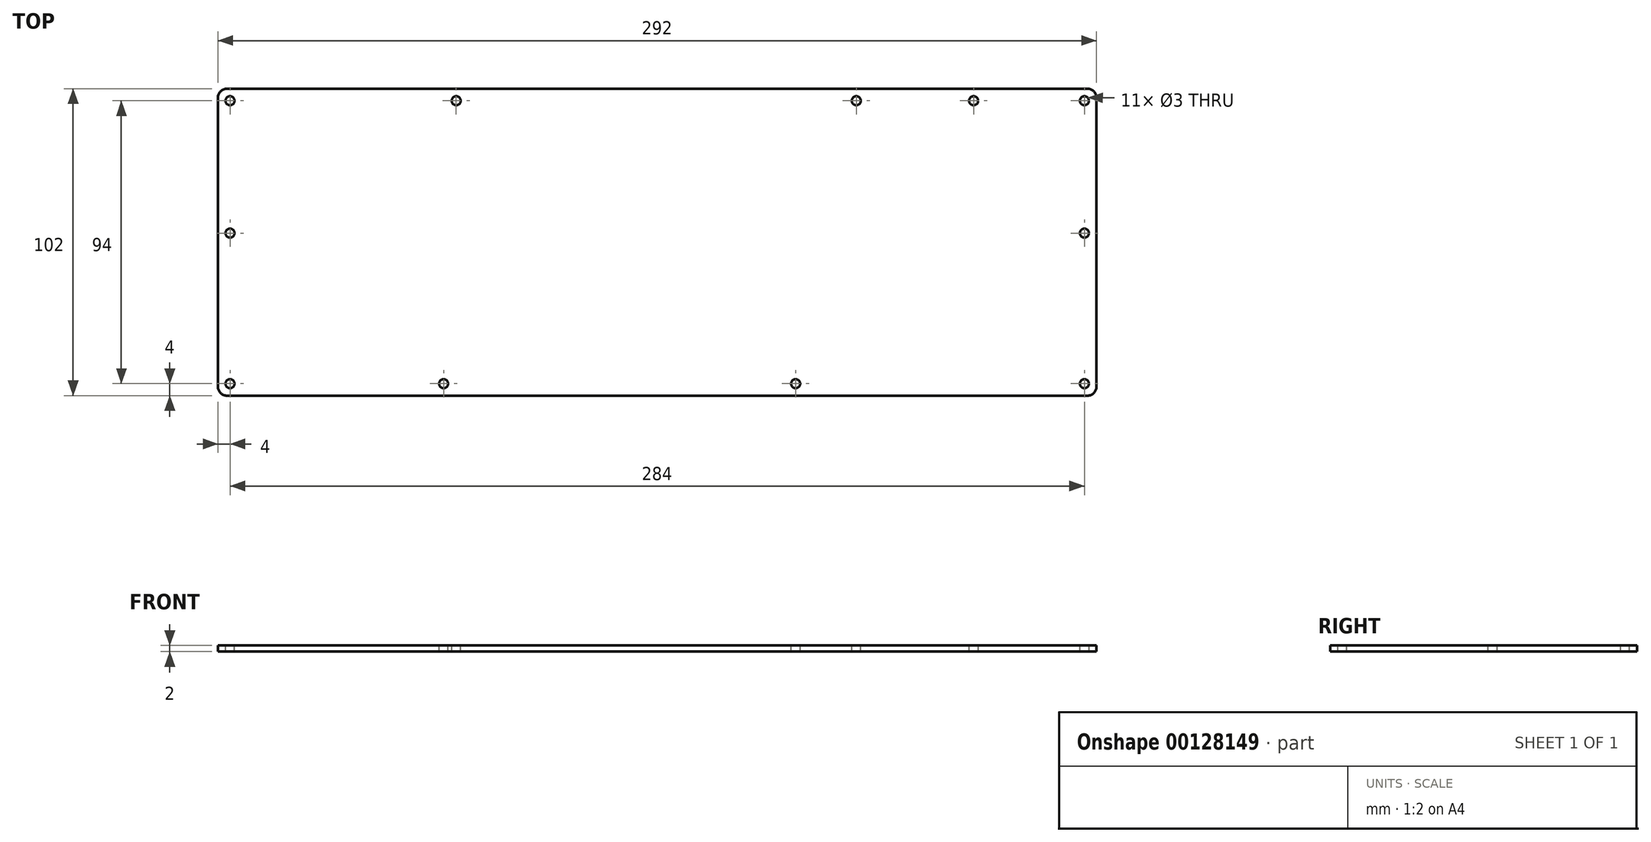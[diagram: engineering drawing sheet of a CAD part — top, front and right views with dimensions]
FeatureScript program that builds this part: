
annotation { "Feature Type Name" : "Feature", "Feature Type Description" : "" }
export const myFeature = defineFeature(function(context is Context, id is Id, definition is map)
    precondition{}
    {
        {
            var Q0;
            Q0=qCreatedBy(makeId("Top.planeOp"),FACE);
            var sketch = newSketch(context, id + "F0", { "sketchPlane" : qUnion([Q0])});
            skLineSegment(sketch, "E0.bottom", {"start": v(143, 51) * mm, "end": v(-143, 51) * mm});
            skLineSegment(sketch, "E0.top", {"start": v(143, -51) * mm, "end": v(-143, -51) * mm});
            skLineSegment(sketch, "E0.left", {"start": v(146, 48) * mm, "end": v(146, -48) * mm});
            skLineSegment(sketch, "E0.right", {"start": v(-146, 48) * mm, "end": v(-146, -48) * mm});
            skPoint(sketch, "E1.visualSharp", {"position": v(-146, 51) * mm});
            skArc(sketch, "E1.filletArc", {"start": v(-143, 51) * mm, "mid": v(-145.12, 50.12) * mm, "end": v(-146, 48) * mm});
            skPoint(sketch, "E2.visualSharp", {"position": v(-146, -51) * mm});
            skArc(sketch, "E2.filletArc", {"start": v(-146, -48) * mm, "mid": v(-145.12, -50.12) * mm, "end": v(-143, -51) * mm});
            skPoint(sketch, "E3.visualSharp", {"position": v(146, -51) * mm});
            skArc(sketch, "E3.filletArc", {"start": v(143, -51) * mm, "mid": v(145.12, -50.12) * mm, "end": v(146, -48) * mm});
            skArc(sketch, "E4.filletArc", {"start": v(146, 48) * mm, "mid": v(145.12, 50.12) * mm, "end": v(143, 51) * mm});
            skSolve(sketch);
        }
        {
            var Q0;
            Q0=qSketchRegion(id+"F0",true);
            extrude(context, id + "F1", {"entities" : qUnion([Q0]), "depth" : 2 * mm});
        }
        {
            var Q0;
            Q0=makeQuery(id+"F1.opExtrude","CAP_FACE",FACE,{"disambiguationData":[OSD([sQuery(id+"F0.wireOp",EDGE,"b1609128-1e4d-4f99-a9c0-d1eb6efb653b"),sQuery(id+"F0.wireOp",EDGE,"f4566b4f-cb64-43fb-b69e-2d4997d02e9e"),sQuery(id+"F0.wireOp",EDGE,"c58de4d6-b1a3-4d1c-92d8-0e596c6fe70e"),sQuery(id+"F0.wireOp",EDGE,"5249d06f-5fa9-4bc2-861d-4cda040d6d12"),sQuery(id+"F0.wireOp",EDGE,"a85e44d5-a424-4784-8d57-3f87bcd3cb1f"),sQuery(id+"F0.wireOp",EDGE,"26f2ad72-3e01-41bb-a775-2f8cfdfabe7d"),sQuery(id+"F0.wireOp",EDGE,"58a866ff-a5cd-410d-a599-dedaca65d45f"),sQuery(id+"F0.wireOp",EDGE,"ffbf0b70-5c72-4423-8b02-8f3d0a3b2328"),sQuery(id+"F0.wireOp",EDGE,"7f67b6f4-1288-461f-aa79-609977e3f21a"),sQuery(id+"F0.wireOp",EDGE,"55541f8a-b999-41dc-948e-6a4feb6e2708"),sQuery(id+"F0.wireOp",EDGE,"6f56692b-9edc-44ed-85e6-53072711c858"),sQuery(id+"F0.wireOp",EDGE,"d64ee7ec-02fb-4461-892d-8620c137c8be"),sQuery(id+"F0.wireOp",EDGE,"a331adab-5858-4e06-9c1d-1ebd579e2d6c"),sQuery(id+"F0.wireOp",EDGE,"872b245d-4d85-40be-bc62-1036af002ab7"),sQuery(id+"F0.wireOp",EDGE,"5f5c10bb-96b1-40b4-bf40-71e8b90fd5b4"),sQuery(id+"F0.wireOp",EDGE,"070c8fee-8489-4fd5-82cc-431f9b446bf5"),sQuery(id+"F0.wireOp",EDGE,"0514bdef-a2e6-47cc-91cb-2d3d024f583d"),sQuery(id+"F0.wireOp",EDGE,"38748b5d-75be-4e41-86c7-7b4e33a636ad"),sQuery(id+"F0.wireOp",EDGE,"ef5fee99-fa31-4ebf-9718-ae6e1dd8c854"),sQuery(id+"F0.wireOp",EDGE,"33aefef2-9a3a-4597-9de5-3f6917e2cb92"),sQuery(id+"F0.wireOp",EDGE,"f576047e-5c30-44eb-8430-c6ba2e10f578"),sQuery(id+"F0.wireOp",EDGE,"5237e12e-b54f-4000-b0ec-e2a188ff4113"),sQuery(id+"F0.wireOp",EDGE,"39a89d85-1c88-4538-9ca2-57a00aa53215"),sQuery(id+"F0.wireOp",EDGE,"1d3d1f3f-65d5-432a-a24c-25425600a27e"),sQuery(id+"F0.wireOp",EDGE,"65133dcd-ba31-495c-9030-11ebdab85244"),sQuery(id+"F0.wireOp",EDGE,"59442c7d-f29c-40c5-8460-04e0c5612805"),sQuery(id+"F0.wireOp",EDGE,"7c508e6d-ace5-438d-ae87-594742bffb03"),sQuery(id+"F0.wireOp",EDGE,"96358abd-ade1-4970-8e96-f48957cb49a9"),sQuery(id+"F0.wireOp",EDGE,"beaf586f-d415-4bcd-bc2c-fe17f6c56d29"),sQuery(id+"F0.wireOp",EDGE,"0b1e909e-c7ab-4355-90a4-b9d381122b20"),sQuery(id+"F0.wireOp",EDGE,"07e25036-969a-447a-8387-7472eab81c53"),sQuery(id+"F0.wireOp",EDGE,"4ac198d4-a843-4e16-ab13-53b4b61c7ec9"),sQuery(id+"F0.wireOp",EDGE,"5899e998-bb7d-4984-919d-5380da3ef46d"),sQuery(id+"F0.wireOp",EDGE,"85bf5025-0c0a-493d-8fd5-15a1002b9e1f"),sQuery(id+"F0.wireOp",EDGE,"433a8b32-5078-4fa2-bccb-dd94966a19e2"),sQuery(id+"F0.wireOp",EDGE,"ca2aed50-1aac-4a88-af60-10e4d26c56ce"),sQuery(id+"F0.wireOp",EDGE,"ad785477-14a5-48c7-ba58-707c46f4f765"),sQuery(id+"F0.wireOp",EDGE,"7e877f2a-03cb-4247-a0d1-3f1f17d45f2e"),sQuery(id+"F0.wireOp",EDGE,"5549e225-b8b0-41a5-a1f6-3a747b09e555"),sQuery(id+"F0.wireOp",EDGE,"7757f798-a692-4454-bd86-5a4d4f9a0c34"),sQuery(id+"F0.wireOp",EDGE,"3016f92a-8452-4434-919c-4a7fc7338035"),sQuery(id+"F0.wireOp",EDGE,"898612aa-0cec-428b-94af-f86252429d12"),sQuery(id+"F0.wireOp",EDGE,"a17dd576-292f-4e6b-9663-d9180f696670"),sQuery(id+"F0.wireOp",EDGE,"cbfd38bd-20b5-4d44-be8c-a17f12e052e0"),sQuery(id+"F0.wireOp",EDGE,"70ab0708-ffdb-4529-bf9e-4018cae3591c"),sQuery(id+"F0.wireOp",EDGE,"f406bcac-c7ef-481d-8174-8bc63e706a56"),sQuery(id+"F0.wireOp",EDGE,"dc331ac5-7670-45e9-89c7-03810e187fe8"),sQuery(id+"F0.wireOp",EDGE,"b3191053-ceed-4c24-bda0-5a50d567a071"),sQuery(id+"F0.wireOp",EDGE,"e110f5b5-6a02-4a34-82cf-196097ccbeb4"),sQuery(id+"F0.wireOp",EDGE,"2b5f7b66-3d2f-406f-a6d7-9a85497eda15"),sQuery(id+"F0.wireOp",EDGE,"76b1751e-cd68-4467-988c-686db3de7683"),sQuery(id+"F0.wireOp",EDGE,"16c5760e-34d5-4e50-8f9d-3caf3d151e1b"),sQuery(id+"F0.wireOp",EDGE,"d295ed9f-bfde-424d-aa21-20497ae6f13c"),sQuery(id+"F0.wireOp",EDGE,"ec12ba42-fae9-4e41-9ad7-bf38757b17f0"),sQuery(id+"F0.wireOp",EDGE,"7436cc0e-6ec4-46fe-a53e-8bd212bcf723"),sQuery(id+"F0.wireOp",EDGE,"0cedb4c9-6a6c-43c2-9996-506471cd3255"),sQuery(id+"F0.wireOp",EDGE,"ec54193d-d4cb-4b1f-86fc-2851957baaba"),sQuery(id+"F0.wireOp",EDGE,"4488f506-9ef2-4267-a6cf-a7b00e78e843"),sQuery(id+"F0.wireOp",EDGE,"372820ab-3034-42cd-b4e6-65ef871f9c40"),sQuery(id+"F0.wireOp",EDGE,"6573e008-ca1a-4dee-91fb-cecced364ef1"),sQuery(id+"F0.wireOp",EDGE,"0ea65bf7-9227-4dbe-9352-82978ca5b32e"),sQuery(id+"F0.wireOp",EDGE,"b1bb12b1-79df-4f2c-a40f-21d0aa567c24"),sQuery(id+"F0.wireOp",EDGE,"0c1536de-d6b0-46e4-9ba7-2841298be202"),sQuery(id+"F0.wireOp",EDGE,"207e1af1-11f0-4a44-9182-2a9f56c0d657"),sQuery(id+"F0.wireOp",EDGE,"27c13fe8-c982-4180-82e1-206dc62b37cb"),sQuery(id+"F0.wireOp",EDGE,"df3f2611-b4d2-4e5e-a9a9-9197ed178f10"),sQuery(id+"F0.wireOp",EDGE,"67ca35e5-e03d-4edf-9133-55c0f28c00dd"),sQuery(id+"F0.wireOp",EDGE,"211b09a9-55cd-462d-ac42-8101b668ed7f"),sQuery(id+"F0.wireOp",EDGE,"3790da84-eb6b-418a-b30a-773cb8711b72"),sQuery(id+"F0.wireOp",EDGE,"8ad775da-4dcc-4f57-b984-0bd12b45c958"),sQuery(id+"F0.wireOp",EDGE,"46f09f23-81b2-4bbc-9572-84064063ea46"),sQuery(id+"F0.wireOp",EDGE,"375117c6-4bbc-4c16-b11f-bde5a02c8ddd"),sQuery(id+"F0.wireOp",EDGE,"edf3fd68-21bd-4dda-b02f-30e2386ebe8c"),sQuery(id+"F0.wireOp",EDGE,"e9b376d0-4e66-4361-894a-f7f99b0a4dba"),sQuery(id+"F0.wireOp",EDGE,"7deef6e9-a95f-4fef-90d6-14df86437aaf"),sQuery(id+"F0.wireOp",EDGE,"3a2c3b9f-72e5-46fb-b22f-c3b3668238e3"),sQuery(id+"F0.wireOp",EDGE,"ef61160d-285f-4999-b3d1-3ad131a5c696"),sQuery(id+"F0.wireOp",EDGE,"5e485a8d-fc2c-447f-9fb7-2a8e8f7db1b8"),sQuery(id+"F0.wireOp",EDGE,"be4b73c1-2188-4d56-b092-b0e9aa332c99"),sQuery(id+"F0.wireOp",EDGE,"7886a41d-8e50-4074-9c4a-38b5df8d299c"),sQuery(id+"F0.wireOp",EDGE,"4e7a6acf-1550-41f7-a348-87a73df4ade2"),sQuery(id+"F0.wireOp",EDGE,"3075fc72-2a9a-4c54-a333-3b9aff6871ba"),sQuery(id+"F0.wireOp",EDGE,"1b470988-ea39-4ef3-b94f-c351ab6970c0"),sQuery(id+"F0.wireOp",EDGE,"d5d0fb32-3312-47e0-b08e-500f4e3a8d6f"),sQuery(id+"F0.wireOp",EDGE,"c95a7a57-a701-41e8-a435-0717771ea27e"),sQuery(id+"F0.wireOp",EDGE,"72f5413f-f806-4961-a1f2-17e8c49a2dbe"),sQuery(id+"F0.wireOp",EDGE,"12295bb0-ec03-4baf-b844-216b01d10c7f"),sQuery(id+"F0.wireOp",EDGE,"ea74abaf-c7a4-4655-a14d-8def43b58c3b"),sQuery(id+"F0.wireOp",EDGE,"fc38e52a-d66c-41f3-a18f-2ab74fc9a3aa"),sQuery(id+"F0.wireOp",EDGE,"b9a872e7-607d-4140-9fac-37e865748f2f"),sQuery(id+"F0.wireOp",EDGE,"469ab4fc-23a3-4a44-8d10-edb1ebb05813"),sQuery(id+"F0.wireOp",EDGE,"6c8f3efd-a16e-4969-a36d-9367de4a04a8"),sQuery(id+"F0.wireOp",EDGE,"d914cece-980e-4aa7-9a19-217e5638b189"),sQuery(id+"F0.wireOp",EDGE,"0d8dcd5d-387b-402a-9c60-ffcbd0bb72cc"),sQuery(id+"F0.wireOp",EDGE,"8cf55217-a1b6-4c1c-9f03-72966d881f0b"),sQuery(id+"F0.wireOp",EDGE,"4053d66f-c8cf-4424-b222-ee203ee23c1e"),sQuery(id+"F0.wireOp",EDGE,"87d9ca37-d664-469b-a4c7-7af1bd52c0ff"),sQuery(id+"F0.wireOp",EDGE,"c0a5d230-8ae8-4271-ac44-5db517de8359"),sQuery(id+"F0.wireOp",EDGE,"1c324c12-bb8f-4aad-bd93-a065141bcc31"),sQuery(id+"F0.wireOp",EDGE,"5157ba3e-39b2-42a3-aeba-34e1f65bc982"),sQuery(id+"F0.wireOp",EDGE,"37ae300f-3520-4053-852e-9cb6712c105c"),sQuery(id+"F0.wireOp",EDGE,"e56d4f24-566a-4093-9c1d-03fa3ce6c3fd"),sQuery(id+"F0.wireOp",EDGE,"c14c5ada-49ad-40e8-9107-312975a1c3f7"),sQuery(id+"F0.wireOp",EDGE,"09f918fb-f6ba-4f35-826c-9be1aaa1e634"),sQuery(id+"F0.wireOp",EDGE,"1a04a7b3-ebb9-45f2-aa82-77a2838be510"),sQuery(id+"F0.wireOp",EDGE,"8b1de847-c452-41c5-811c-5ab6a2f757b0"),sQuery(id+"F0.wireOp",EDGE,"07133ebf-dc20-4f31-a97c-dbe7588edc2e"),sQuery(id+"F0.wireOp",EDGE,"82b11f7f-3426-4d96-a479-9e8199cbbcbe"),sQuery(id+"F0.wireOp",EDGE,"692c3182-390b-47c5-b81b-f7c9554c5188"),sQuery(id+"F0.wireOp",EDGE,"ec9cd909-a83d-4db2-80ed-a48da1c01f2a"),sQuery(id+"F0.wireOp",EDGE,"8999d2ee-b3fd-40a3-91db-70ba8707524c"),sQuery(id+"F0.wireOp",EDGE,"877071da-4e0e-44ee-80f9-18e6a312fe40"),sQuery(id+"F0.wireOp",EDGE,"310de26f-e1f4-4f76-a7a2-31cd6309eb9f"),sQuery(id+"F0.wireOp",EDGE,"ad3c8448-077b-42fa-b66f-cb204dd4b24b"),sQuery(id+"F0.wireOp",EDGE,"dc182899-f22f-43ca-bb7a-d9cff2bb14a0"),sQuery(id+"F0.wireOp",EDGE,"65f270fc-c84c-425a-8765-446292cb4d3e"),sQuery(id+"F0.wireOp",EDGE,"c2b09f90-88b6-4d72-8a72-16f5e25146eb"),sQuery(id+"F0.wireOp",EDGE,"c2295a2a-ded6-4c6f-a2aa-a895bf3941d7"),sQuery(id+"F0.wireOp",EDGE,"c37eb4cb-c588-4c6c-82ac-1d42e178e50a"),sQuery(id+"F0.wireOp",EDGE,"c6fafc2d-4fcb-4607-9bd2-8190c812e452"),sQuery(id+"F0.wireOp",EDGE,"9417043a-912b-430b-98cd-4ce252294d8a"),sQuery(id+"F0.wireOp",EDGE,"25218a79-4e2b-4d76-88a5-5a80dd25db46"),sQuery(id+"F0.wireOp",EDGE,"52fe2f22-f5c3-47de-b85b-7071680885e1"),sQuery(id+"F0.wireOp",EDGE,"8db425a6-9809-493b-a625-842b3707d4f8"),sQuery(id+"F0.wireOp",EDGE,"108efb8e-72e4-46dc-b29e-3530763ab2cb"),sQuery(id+"F0.wireOp",EDGE,"37e6c475-f92b-460d-bb35-4d3434045b59"),sQuery(id+"F0.wireOp",EDGE,"41b95ee3-14c1-4901-89de-568e1f007773"),sQuery(id+"F0.wireOp",EDGE,"01807cc5-b0aa-4840-a249-294bda683d07"),sQuery(id+"F0.wireOp",EDGE,"152e1f9d-8930-4523-a05f-674d844d7707"),sQuery(id+"F0.wireOp",EDGE,"5efd5115-699b-4425-b653-4cc125bcd7d7"),sQuery(id+"F0.wireOp",EDGE,"1cc39329-d833-44ea-a2f6-ea7c9f78653e"),sQuery(id+"F0.wireOp",EDGE,"0dca4560-2abc-4104-80a8-7adf0bc88beb"),sQuery(id+"F0.wireOp",EDGE,"6916323c-6478-4019-a811-1e709e75c72c"),sQuery(id+"F0.wireOp",EDGE,"2451c855-d06f-4170-a402-bb45c563284a"),sQuery(id+"F0.wireOp",EDGE,"8586e523-ca72-4acf-a6f5-917adcdadd36"),sQuery(id+"F0.wireOp",EDGE,"930f09bf-785d-44d0-a635-5104e1f2550d"),sQuery(id+"F0.wireOp",EDGE,"c441b449-73cf-46cf-ad09-9110f26cec35"),sQuery(id+"F0.wireOp",EDGE,"60176a13-c84b-409f-9b5c-2d317961481d"),sQuery(id+"F0.wireOp",EDGE,"fc777e31-b308-4b5e-985b-35cb478bdecb"),sQuery(id+"F0.wireOp",EDGE,"e88cf7bc-e46a-4de7-95e0-dad1476bcc0c"),sQuery(id+"F0.wireOp",EDGE,"96c8cf9e-4ec9-44d1-ad91-7186c6f1f209"),sQuery(id+"F0.wireOp",EDGE,"658329ac-6692-4e40-9ef8-a494bcb0f754"),sQuery(id+"F0.wireOp",EDGE,"d67bae1f-3ffd-4beb-8cc6-29e61c8b342c"),sQuery(id+"F0.wireOp",EDGE,"dbf715f9-25b6-4774-be77-851613eb5e25"),sQuery(id+"F0.wireOp",EDGE,"d8d12f8c-32ed-4466-a5bc-cbc1cfba4feb"),sQuery(id+"F0.wireOp",EDGE,"4beba3b0-c51b-4a43-948d-e7233947d5dc"),sQuery(id+"F0.wireOp",EDGE,"fcfcb946-a851-45fe-a21c-e3f885e48000"),sQuery(id+"F0.wireOp",EDGE,"4d44fab2-dba1-4fbc-848d-77cfe8fac08b"),sQuery(id+"F0.wireOp",EDGE,"5776a788-e3c3-4dac-aeb6-7777a672858e"),sQuery(id+"F0.wireOp",EDGE,"cedf499e-2994-4c9b-b766-b127bb67c415"),sQuery(id+"F0.wireOp",EDGE,"0a2e2db6-b390-46fd-b74c-53757edf0af6"),sQuery(id+"F0.wireOp",EDGE,"4ce94d68-acc0-4cfe-bd55-ec03fe200a5b"),sQuery(id+"F0.wireOp",EDGE,"e0c07793-b957-4333-96dc-a294f1e2ceb0"),sQuery(id+"F0.wireOp",EDGE,"41979a11-f1a0-4749-a17a-603b7864cc01"),sQuery(id+"F0.wireOp",EDGE,"aa3ca26f-036c-439d-b566-5430048ebdf9"),sQuery(id+"F0.wireOp",EDGE,"249b810b-8968-482f-8bbc-e4399ea1180f"),sQuery(id+"F0.wireOp",EDGE,"3f1de34e-7a13-4160-8f1e-59d99b5a4c3a"),sQuery(id+"F0.wireOp",EDGE,"f0e1049c-435a-4f02-948e-5f98f668222f"),sQuery(id+"F0.wireOp",EDGE,"dceacdf6-e703-4809-b70b-d17cfe04b7d7"),sQuery(id+"F0.wireOp",EDGE,"bdd4c6ec-239a-424d-8041-67786f5d4ce7"),sQuery(id+"F0.wireOp",EDGE,"44e7c303-723b-4c42-a54a-8f557ff9a9f6"),sQuery(id+"F0.wireOp",EDGE,"e59f6ee7-3ba8-4e2b-b5d6-6e605825de7d"),sQuery(id+"F0.wireOp",EDGE,"3867d971-9346-4093-a9b2-274161278cdc"),sQuery(id+"F0.wireOp",EDGE,"d52ba1ae-d7a3-467c-9b67-1ae8c09bf28e"),sQuery(id+"F0.wireOp",EDGE,"1800a961-f957-4766-bec1-88f23ee5c048"),sQuery(id+"F0.wireOp",EDGE,"944022d4-31d1-4345-9843-0181748df1e1"),sQuery(id+"F0.wireOp",EDGE,"56ca7d79-5fc4-42fd-843a-33c232b6b3c3"),sQuery(id+"F0.wireOp",EDGE,"098c2286-8095-4fed-8dd0-5a8dec876cb3"),sQuery(id+"F0.wireOp",EDGE,"2ad36734-b040-4264-b8f6-ee2da5387eb9"),sQuery(id+"F0.wireOp",EDGE,"ccc487cc-2c29-4e42-a366-3ba57780b9a2"),sQuery(id+"F0.wireOp",EDGE,"7b328234-d38a-4842-b15d-1fbe1fd70208"),sQuery(id+"F0.wireOp",EDGE,"3732f762-4107-4d06-83e4-c8630a2c37fb"),sQuery(id+"F0.wireOp",EDGE,"8b64106c-834e-4e21-a7c0-f3940f540fb2"),sQuery(id+"F0.wireOp",EDGE,"6e7361da-996f-46b3-a434-00db9b4c9c9f"),sQuery(id+"F0.wireOp",EDGE,"b0b43ae6-5ac0-41e1-a04e-e485c33c99f8"),sQuery(id+"F0.wireOp",EDGE,"db5e65e6-5182-4048-9572-11a43cb11c51"),sQuery(id+"F0.wireOp",EDGE,"26e7e85a-b403-48fa-8c29-07448647ad8f"),sQuery(id+"F0.wireOp",EDGE,"515b21e0-8220-4d96-96a0-4c14be87b64b"),sQuery(id+"F0.wireOp",EDGE,"aa12bfdd-f8d8-4067-91a8-122e35d45f26"),sQuery(id+"F0.wireOp",EDGE,"9aa84255-1989-40c3-bf0d-31009647c77f"),sQuery(id+"F0.wireOp",EDGE,"aa9638c1-c68d-45f6-940c-d0f327c0fa45"),sQuery(id+"F0.wireOp",EDGE,"251b7c26-2c5b-48f1-8bde-e20a856a34ff"),sQuery(id+"F0.wireOp",EDGE,"18e7e5a9-24b2-485b-ab29-6ec4d7284516"),sQuery(id+"F0.wireOp",EDGE,"f4cd6263-1ac9-4123-a1aa-8b6f3d1fe724"),sQuery(id+"F0.wireOp",EDGE,"34207eab-8dad-445e-ac2c-5e7baad48e02"),sQuery(id+"F0.wireOp",EDGE,"d2cd9a5c-99c8-49cb-9122-6c3893475af4"),sQuery(id+"F0.wireOp",EDGE,"0ab99930-a22d-41a5-8d7a-f072e43d683d"),sQuery(id+"F0.wireOp",EDGE,"ba1f877b-ae2d-41b0-a78f-99f645971353"),sQuery(id+"F0.wireOp",EDGE,"7655611b-0d56-496a-9af6-17078dfc8983"),sQuery(id+"F0.wireOp",EDGE,"2217c71d-48f5-44f0-b6aa-e70c41dec14e"),sQuery(id+"F0.wireOp",EDGE,"2da62ed5-bda3-4005-8c82-b2de019464e8"),sQuery(id+"F0.wireOp",EDGE,"b9e5db85-9e65-4104-9569-ca807059eb4d"),sQuery(id+"F0.wireOp",EDGE,"e8855f58-9b24-4e18-bc1c-a0daeed810ba"),sQuery(id+"F0.wireOp",EDGE,"6c73f8f0-d719-4729-89df-4c554db3bf8c"),sQuery(id+"F0.wireOp",EDGE,"99502265-d697-4b9c-a12a-a7646a77523d"),sQuery(id+"F0.wireOp",EDGE,"5ad33bb7-7d8c-4f73-a2bd-749fa85a955e"),sQuery(id+"F0.wireOp",EDGE,"ffa3529a-edc2-4b05-9642-06e0e9a42b66"),sQuery(id+"F0.wireOp",EDGE,"221bf0c5-454d-44e2-b718-00ef1a2cf6b4"),sQuery(id+"F0.wireOp",EDGE,"2bf5e5ca-39b4-4044-8377-129965e258c5"),sQuery(id+"F0.wireOp",EDGE,"ba879806-eb56-4bd7-bf01-18ec1c857bc0"),sQuery(id+"F0.wireOp",EDGE,"64b71d1f-be08-4438-bafa-bb0b385583c3"),sQuery(id+"F0.wireOp",EDGE,"9a261f28-0ea3-4c64-a250-fe02b8de4198"),sQuery(id+"F0.wireOp",EDGE,"9c6a15b5-d89c-4f27-9035-4432c0c29f03"),sQuery(id+"F0.wireOp",EDGE,"39fc6f70-527d-491a-b3cc-87afca1fd921"),sQuery(id+"F0.wireOp",EDGE,"83ff7e70-d247-44e0-9e1a-45f528f1984e"),sQuery(id+"F0.wireOp",EDGE,"8c19abdc-fab5-49c6-a1e3-3ac5321561f2"),sQuery(id+"F0.wireOp",EDGE,"38f5175e-ca97-4091-a899-2fc862d9fcf7"),sQuery(id+"F0.wireOp",EDGE,"a6b59a2b-11a6-4381-9ec9-9e4786140b61"),sQuery(id+"F0.wireOp",EDGE,"a6aa3d57-10a3-484e-8f69-3d26024ead90"),sQuery(id+"F0.wireOp",EDGE,"cab9f132-7f02-4cf2-a837-44b314ab0f2d"),sQuery(id+"F0.wireOp",EDGE,"4d87c6e3-345b-4698-85be-4c1066c996ba"),sQuery(id+"F0.wireOp",EDGE,"100f6826-a35e-44dc-8f5e-91e6494c0734"),sQuery(id+"F0.wireOp",EDGE,"6b51b95a-e805-4a4c-b3ce-42549b1f7c4f"),sQuery(id+"F0.wireOp",EDGE,"4974438e-2757-4174-b66e-648bb066325b"),sQuery(id+"F0.wireOp",EDGE,"06557fa0-7690-4017-ac39-cec9dddb7ac3"),sQuery(id+"F0.wireOp",EDGE,"190d5702-5898-49b5-8b03-446313d35a85"),sQuery(id+"F0.wireOp",EDGE,"13d402cf-df92-4d9a-ac9d-1f67946c0a84"),sQuery(id+"F0.wireOp",EDGE,"2f2b7a4a-fe61-4bf2-9a19-afa51de3c721"),sQuery(id+"F0.wireOp",EDGE,"89631652-7db3-4c6b-99e7-db613ff7bbbb"),sQuery(id+"F0.wireOp",EDGE,"9bb81fc8-ca7b-4002-871d-2f89aed8432f"),sQuery(id+"F0.wireOp",EDGE,"a13c4922-8a72-4012-be87-7b5d4d768a52"),sQuery(id+"F0.wireOp",EDGE,"2badb0fd-de87-488b-8ff2-1cf5654be30e"),sQuery(id+"F0.wireOp",EDGE,"3885baab-ef1d-4d35-a85f-7a32c066c2bb"),sQuery(id+"F0.wireOp",EDGE,"5dec05d8-971c-49fe-8ee5-de689f2777ed"),sQuery(id+"F0.wireOp",EDGE,"4173ea56-7147-43d2-9c71-5769336bf9f5"),sQuery(id+"F0.wireOp",EDGE,"ac75d90e-cfd8-4d37-ba29-49a000d3f1ae"),sQuery(id+"F0.wireOp",EDGE,"98559af5-3831-4093-9a27-000fd7a0f36c"),sQuery(id+"F0.wireOp",EDGE,"e31d4e9e-ec26-4480-9e00-58e09570ae7e"),sQuery(id+"F0.wireOp",EDGE,"e82aada4-95ef-49cd-9523-bf5d0496c439"),sQuery(id+"F0.wireOp",EDGE,"21f6afce-f90f-4921-86bd-c08a04096671"),sQuery(id+"F0.wireOp",EDGE,"3c7f96f7-af1a-4bca-82d7-7f24edd57999"),sQuery(id+"F0.wireOp",EDGE,"9c442e46-f741-49c2-ae82-587b697e79f8"),sQuery(id+"F0.wireOp",EDGE,"f57068b1-2418-4c58-9872-b1a6e01bfd01"),sQuery(id+"F0.wireOp",EDGE,"aca98637-d3dc-411b-a35d-96c25150bc33"),sQuery(id+"F0.wireOp",EDGE,"d832a37b-e081-415c-bcce-cbaaf2c07a6e"),sQuery(id+"F0.wireOp",EDGE,"c9b6084d-535c-4eea-879b-8436754e0a02"),sQuery(id+"F0.wireOp",EDGE,"83c218aa-2010-4a7a-b09b-f6f7594d2848"),sQuery(id+"F0.wireOp",EDGE,"25d1440d-df07-499d-9911-16ffe4e38f84"),sQuery(id+"F0.wireOp",EDGE,"b6ddaadb-7141-4236-b186-f6da43c88cd6"),sQuery(id+"F0.wireOp",EDGE,"31b5fb8c-a189-40bf-8a18-47b0cc85132f"),sQuery(id+"F0.wireOp",EDGE,"37fcbbbc-e4b3-40ea-a50b-883800e78a5e"),sQuery(id+"F0.wireOp",EDGE,"d3f70543-5bb9-47e1-870b-7f1758817613"),sQuery(id+"F0.wireOp",EDGE,"f9c8d4e8-c029-4b82-b080-4960ce172a88"),sQuery(id+"F0.wireOp",EDGE,"39afe83d-89d6-44e1-8ada-1b9ab1a1485e"),sQuery(id+"F0.wireOp",EDGE,"a4da8c96-5464-43a0-a877-97641311b988"),sQuery(id+"F0.wireOp",EDGE,"501f0886-9544-46dc-adfd-6bdb9374b70b"),sQuery(id+"F0.wireOp",EDGE,"a040e1e7-e6a2-42d4-8a0a-b58d54095c78"),sQuery(id+"F0.wireOp",EDGE,"266685c9-b8b4-4f14-8dcb-010c88eb1083"),sQuery(id+"F0.wireOp",EDGE,"a78f4bb4-8cf1-45b3-bd54-ed21ce6b7e77"),sQuery(id+"F0.wireOp",EDGE,"9fed2e65-49e2-48d5-91fd-bef8366991b9"),sQuery(id+"F0.wireOp",EDGE,"e5b929db-a2ea-4433-8172-c9d0a43971ef"),sQuery(id+"F0.wireOp",EDGE,"d15be14e-e4f7-4dc7-82c5-c08f03b6a96b"),sQuery(id+"F0.wireOp",EDGE,"4e03f35e-05bc-4b6a-8889-a9f08c83d29e"),sQuery(id+"F0.wireOp",EDGE,"d6bfbf06-55c8-4808-983c-7f728cc75ab0"),sQuery(id+"F0.wireOp",EDGE,"625082b8-4dc8-485c-a11f-6dd84b90f705"),sQuery(id+"F0.wireOp",EDGE,"6e6ef2d8-6f26-4221-b3c2-0aed2e8eeeea"),sQuery(id+"F0.wireOp",EDGE,"fde2ada2-eb67-4ef0-beec-9eb2ee9529bd"),sQuery(id+"F0.wireOp",EDGE,"ff846ca3-1931-47eb-b30c-d282e952b59a"),sQuery(id+"F0.wireOp",EDGE,"2f7f04d9-0a77-41a9-a710-5b10e0b304b1"),sQuery(id+"F0.wireOp",EDGE,"7ec9521f-18ef-41a3-8966-0f2aee6ff685"),sQuery(id+"F0.wireOp",EDGE,"b32b4623-d4c6-405e-ac90-b876da4664bc"),sQuery(id+"F0.wireOp",EDGE,"e1e232c8-27d0-46d2-b10c-53b0933a74ee"),sQuery(id+"F0.wireOp",EDGE,"4dc7a203-5312-4640-a274-b1f682c48a83"),sQuery(id+"F0.wireOp",EDGE,"5ec18aa4-844b-4fd6-bb0f-ea66bd33227a"),sQuery(id+"F0.wireOp",EDGE,"82f6a369-effc-4e42-8078-1b4068fc9ca4"),sQuery(id+"F0.wireOp",EDGE,"1d6cbc2a-f3a5-4e8c-9653-84e9777b349f"),sQuery(id+"F0.wireOp",EDGE,"394b4bd7-1cda-4ff6-a125-fc6477bc39fb"),sQuery(id+"F0.wireOp",EDGE,"57d5dcee-28cf-4cba-8a40-e39ca4d8f1a1"),sQuery(id+"F0.wireOp",EDGE,"dc2c0885-5591-4e00-be3a-884cbec6d151"),sQuery(id+"F0.wireOp",EDGE,"aad2d9a4-5522-4183-a005-46352570c096"),sQuery(id+"F0.wireOp",EDGE,"ab95f565-e86b-404d-b46e-959ec70fe326"),sQuery(id+"F0.wireOp",EDGE,"1a3e4d60-116d-4e15-acde-dbb54cdc3e9f"),sQuery(id+"F0.wireOp",EDGE,"2f20cbd4-76e3-4f74-8986-d968588fc4e8"),sQuery(id+"F0.wireOp",EDGE,"753a2c14-8ac4-46b1-adcd-2c7270b5770b"),sQuery(id+"F0.wireOp",EDGE,"6aad7a9e-0483-4a9a-9044-6663aff9a316"),sQuery(id+"F0.wireOp",EDGE,"0a2596d7-6d10-47f5-a9f2-89b9bf7a1f87"),sQuery(id+"F0.wireOp",EDGE,"85a143d8-6ea7-4fbd-94c9-d270f6c85c66"),sQuery(id+"F0.wireOp",EDGE,"8d7e53f5-cfe5-40a6-8ffa-4bf0b95a127d"),sQuery(id+"F0.wireOp",EDGE,"3fd28192-c398-4a49-a92d-335951c4506c"),sQuery(id+"F0.wireOp",EDGE,"17979889-b5c4-4d1c-9b8a-43c43d671ab6"),sQuery(id+"F0.wireOp",EDGE,"92f33dad-6f90-4d6e-b4ec-202fb2800c95"),sQuery(id+"F0.wireOp",EDGE,"0ab45290-3409-407a-97d1-1798937913bc"),sQuery(id+"F0.wireOp",EDGE,"2c5f605b-9cbf-444f-b4f0-d3661b8886fe"),sQuery(id+"F0.wireOp",EDGE,"b840f495-8230-455c-8c8f-9fcbc6fdd650"),sQuery(id+"F0.wireOp",EDGE,"9ef30627-d4f6-40fe-a0c9-13aa0f7e93fc"),sQuery(id+"F0.wireOp",EDGE,"4461d5c2-7a67-47f2-8962-6c99b4a5204c"),sQuery(id+"F0.wireOp",EDGE,"081d79c5-aad2-40dd-bb6e-7a0aabafd1b6"),sQuery(id+"F0.wireOp",EDGE,"f9e75d03-768d-470f-8f10-b6e003a855e7"),sQuery(id+"F0.wireOp",EDGE,"4c0c9c3d-329b-4999-a02d-13464766462d"),sQuery(id+"F0.wireOp",EDGE,"7b7e0f44-dbb4-4f47-be36-2e83010483bd"),sQuery(id+"F0.wireOp",EDGE,"1e10e814-c332-4ecf-91b1-3ebca5584570"),sQuery(id+"F0.wireOp",EDGE,"59ac1f3f-6679-4629-b80b-61bd17a2b2f8"),sQuery(id+"F0.wireOp",EDGE,"ae25387f-1f81-4d49-9314-d22d11f38b5d"),sQuery(id+"F0.wireOp",EDGE,"305fb3d6-1341-4639-b3e8-1374f76d0736"),sQuery(id+"F0.wireOp",EDGE,"8d6a009a-bdc3-4505-b116-9dfb21e65cd5"),sQuery(id+"F0.wireOp",EDGE,"e117250e-32e6-4a26-86f8-0e13f4d16bec"),sQuery(id+"F0.wireOp",EDGE,"41386a07-9f86-4093-b2d2-7aa4842ce662"),sQuery(id+"F0.wireOp",EDGE,"9c5f58e5-8954-465d-9504-48b7d980ba6b"),sQuery(id+"F0.wireOp",EDGE,"56670a70-7e0d-4b80-9dd5-68985d74d020"),sQuery(id+"F0.wireOp",EDGE,"8ce40b0d-489f-4ffc-a366-aa5d5dbd9682"),sQuery(id+"F0.wireOp",EDGE,"9cafe44c-6f76-40ea-9fd8-f282bb15773c"),sQuery(id+"F0.wireOp",EDGE,"a5e7a8d2-c55f-494a-9a49-f046675af114"),sQuery(id+"F0.wireOp",EDGE,"1bec7831-0536-4ac3-afc2-476294aa08ed"),sQuery(id+"F0.wireOp",EDGE,"fa5222d6-37b7-4824-9e79-5f0c5d09a009"),sQuery(id+"F0.wireOp",EDGE,"b3891244-9859-4daf-be27-380808788fd3"),sQuery(id+"F0.wireOp",EDGE,"c7feb413-078f-49a4-85ea-459ed2746111"),sQuery(id+"F0.wireOp",EDGE,"b0081492-be99-4dc3-b230-7d0aab91f03c"),sQuery(id+"F0.wireOp",EDGE,"7edeb0e6-a732-4e48-a81b-608c459c7c27"),sQuery(id+"F0.wireOp",EDGE,"867c9e95-7424-4e1d-87d8-b22a68c3c025"),sQuery(id+"F0.wireOp",EDGE,"9c27c829-7a0d-4637-b876-c453130a447f"),sQuery(id+"F0.wireOp",EDGE,"d3c4b1f1-9457-4f91-b126-2c4e7d60c85a"),sQuery(id+"F0.wireOp",EDGE,"22a6e6f7-cc3c-41fb-9e90-cc46def12613"),sQuery(id+"F0.wireOp",EDGE,"83a76977-9a06-423b-ae66-cd00626cf560"),sQuery(id+"F0.wireOp",EDGE,"3f29e2a1-a5c9-4722-b659-4ee6781ed382"),sQuery(id+"F0.wireOp",EDGE,"fd5f3ce2-0948-486b-aa29-b785551bf386"),sQuery(id+"F0.wireOp",EDGE,"7599906f-92b1-4219-8dd3-bf5d8a31e626"),sQuery(id+"F0.wireOp",EDGE,"2add90be-772b-4aa5-b982-7332210cce71"),sQuery(id+"F0.wireOp",EDGE,"2a6877ed-6dab-4773-a72d-47a1a77d2c9f"),sQuery(id+"F0.wireOp",EDGE,"4cbb10b3-3aa2-4e86-8ee4-578b1c38922a"),sQuery(id+"F0.wireOp",EDGE,"ffd5fb1b-367a-48dc-84a3-11640e968880"),sQuery(id+"F0.wireOp",EDGE,"b6fbc371-c7be-499f-aee2-95a98a174042"),sQuery(id+"F0.wireOp",EDGE,"412ed036-02e6-436f-ba39-a533e7d8d566"),sQuery(id+"F0.wireOp",EDGE,"c40d6e9d-23c6-4394-82e4-2dcbbd49f451"),sQuery(id+"F0.wireOp",EDGE,"57b9e075-483a-4aa5-9f8d-aed7ae9a4015"),sQuery(id+"F0.wireOp",EDGE,"7a8d3c14-78e7-4489-a911-4a74efbfc4b3"),sQuery(id+"F0.wireOp",EDGE,"09ad2b53-dbf9-4d92-8b7e-6870fa5a446d"),sQuery(id+"F0.wireOp",EDGE,"1f6abc6c-9e44-49fd-bf99-f16bc5950d3f"),sQuery(id+"F0.wireOp",EDGE,"f41b703e-44d6-4482-948b-e04385fb91a8"),sQuery(id+"F0.wireOp",EDGE,"91d70adb-115e-4ffb-a395-2b6cacca741c"),sQuery(id+"F0.wireOp",EDGE,"dda57363-ed32-4561-a2c0-083cdafd8a37"),sQuery(id+"F0.wireOp",EDGE,"7a3fefc2-0a72-4021-b326-2823abfe09e3"),sQuery(id+"F0.wireOp",EDGE,"4b5e01bc-3fbf-4abe-aed3-b0d3e09be2f4"),sQuery(id+"F0.wireOp",EDGE,"0a378d94-3c4a-453d-92a8-3da6627ba44f"),sQuery(id+"F0.wireOp",EDGE,"96939f80-8f1b-456a-a56f-a45e4b84fff2"),sQuery(id+"F0.wireOp",EDGE,"8690dbd8-32d0-4c24-9a6f-21ccdc6d1b7b"),sQuery(id+"F0.wireOp",EDGE,"41a9296a-9171-4399-88f5-af94295a5342"),sQuery(id+"F0.wireOp",EDGE,"de1af690-d43f-4b9a-858b-9be29a448911"),sQuery(id+"F0.wireOp",EDGE,"edbdedd4-bb9a-406e-9dd7-aaae3bf236ae"),sQuery(id+"F0.wireOp",EDGE,"d51c5f01-75a1-4b6c-a957-fca7eef8146b"),sQuery(id+"F0.wireOp",EDGE,"b3fd92ac-78b6-41b1-afc0-ee29ddcca53f"),sQuery(id+"F0.wireOp",EDGE,"2cda1eef-ec72-41ac-bce3-61a85240fdd5"),sQuery(id+"F0.wireOp",EDGE,"71c48189-8c54-4eb2-a12e-6105fa345c64"),sQuery(id+"F0.wireOp",EDGE,"9f1062f6-9304-4d8d-9ce9-abb74b2d722e"),sQuery(id+"F0.wireOp",EDGE,"bf896698-4176-4980-b20a-78c865a3d341"),sQuery(id+"F0.wireOp",EDGE,"b7b6dc4d-cf79-4355-b5e9-8fde5f500ec0"),sQuery(id+"F0.wireOp",EDGE,"7f73ae36-54b1-49d6-8841-5560dfb65061"),sQuery(id+"F0.wireOp",EDGE,"62dbb698-6cc5-4ac8-9783-cd1c26481057"),sQuery(id+"F0.wireOp",EDGE,"a9b6f9ac-2563-4c2d-9a9e-898be4e77e27"),sQuery(id+"F0.wireOp",EDGE,"b748b83c-cc52-469c-b6c0-f44465017a8c"),sQuery(id+"F0.wireOp",EDGE,"c8facb2b-b026-4934-a63b-b5607b87cb66"),sQuery(id+"F0.wireOp",EDGE,"cfe49408-1198-43da-bc37-20620b43ecba"),sQuery(id+"F0.wireOp",EDGE,"c7d4460d-85fc-4d6f-b61a-7110802d6a6a"),sQuery(id+"F0.wireOp",EDGE,"1b071a63-40b8-4c94-9dfb-8e2c33fe026c"),sQuery(id+"F0.wireOp",EDGE,"5085e82c-c506-464d-9a31-33060296f019"),sQuery(id+"F0.wireOp",EDGE,"f39580b1-4943-4daa-9aeb-e63f821f6646"),sQuery(id+"F0.wireOp",EDGE,"faafab1b-27c7-4fec-a70a-5a6f0e2d9a62"),sQuery(id+"F0.wireOp",EDGE,"db622875-df72-4ad8-b8c4-500b0e330896"),sQuery(id+"F0.wireOp",EDGE,"680b1a25-a5b3-435f-962b-75b95a27b20f"),sQuery(id+"F0.wireOp",EDGE,"9615cfa5-d949-43e5-b88d-47ba86214343"),sQuery(id+"F0.wireOp",EDGE,"c9b12d91-4184-4bdc-82a4-c7504ad794e0"),sQuery(id+"F0.wireOp",EDGE,"856246d2-e0bf-4f01-aded-4de051bcbc94"),sQuery(id+"F0.wireOp",EDGE,"f6dddd8d-1894-43b6-a926-3e2663eaabd2"),sQuery(id+"F0.wireOp",EDGE,"b1722177-dd49-41cd-ad15-c1adc430affd"),sQuery(id+"F0.wireOp",EDGE,"efb29aa0-0f38-401f-89a6-a67a7e04fdcb"),sQuery(id+"F0.wireOp",EDGE,"681c5269-f780-41cb-9872-6f5a5ac3c074"),sQuery(id+"F0.wireOp",EDGE,"e9f3e534-2fe3-4adf-b3b3-a70aa0e0abbc"),sQuery(id+"F0.wireOp",EDGE,"184a51fd-37f7-4e2e-8b20-b78d3d228c3e"),sQuery(id+"F0.wireOp",EDGE,"c8e7bc03-7667-4963-ac8a-0e4c5ad09257"),sQuery(id+"F0.wireOp",EDGE,"2684f396-274b-4407-9748-250128256beb"),sQuery(id+"F0.wireOp",EDGE,"cb26cbe6-b294-4172-807b-7e2fe063b7af"),sQuery(id+"F0.wireOp",EDGE,"373a3cfd-3014-4e28-9adb-c235d9bd59d7"),sQuery(id+"F0.wireOp",EDGE,"faf1a0ad-00b5-4abd-ba04-7585af7e1ba0"),sQuery(id+"F0.wireOp",EDGE,"E0.bottom"),sQuery(id+"F0.wireOp",EDGE,"E0.top"),sQuery(id+"F0.wireOp",EDGE,"E0.left"),sQuery(id+"F0.wireOp",EDGE,"E0.right")])],"isStart":false});
            var sketch = newSketch(context, id + "F2", { "sketchPlane" : qUnion([Q0])});
            skCircle(sketch, "E5", {"center": v(-142, 47) * mm, "radius": 1.5 * mm});
            skCircle(sketch, "E6", {"center": v(142, 47) * mm, "radius": 1.5 * mm});
            skCircle(sketch, "E7", {"center": v(-66.83, 47) * mm, "radius": 1.5 * mm});
            skCircle(sketch, "E8", {"center": v(66.17, 47) * mm, "radius": 1.5 * mm});
            skCircle(sketch, "E9", {"center": v(-142, -47) * mm, "radius": 1.5 * mm});
            skCircle(sketch, "E10", {"center": v(142, -47) * mm, "radius": 1.5 * mm});
            skCircle(sketch, "E11", {"center": v(-71, -47) * mm, "radius": 1.5 * mm});
            skCircle(sketch, "E12", {"center": v(46, -47) * mm, "radius": 1.5 * mm});
            skCircle(sketch, "E13", {"center": v(142, 3) * mm, "radius": 1.5 * mm});
            skCircle(sketch, "E14", {"center": v(-142, 3) * mm, "radius": 1.5 * mm});
            skCircle(sketch, "E15", {"center": v(105.17, 47) * mm, "radius": 1.5 * mm});
            skSolve(sketch);
        }
        {
            var Q0;
            Q0=qSketchRegion(id+"F2",true);
            extrude(context, id + "F3", {"entities" : qUnion([Q0]), "operationType" : NewBodyOperationType.REMOVE, "endBound" : BoundingType.THROUGH_ALL, "oppositeDirection" : true, "depth" : 25 * mm});
        }
    });
